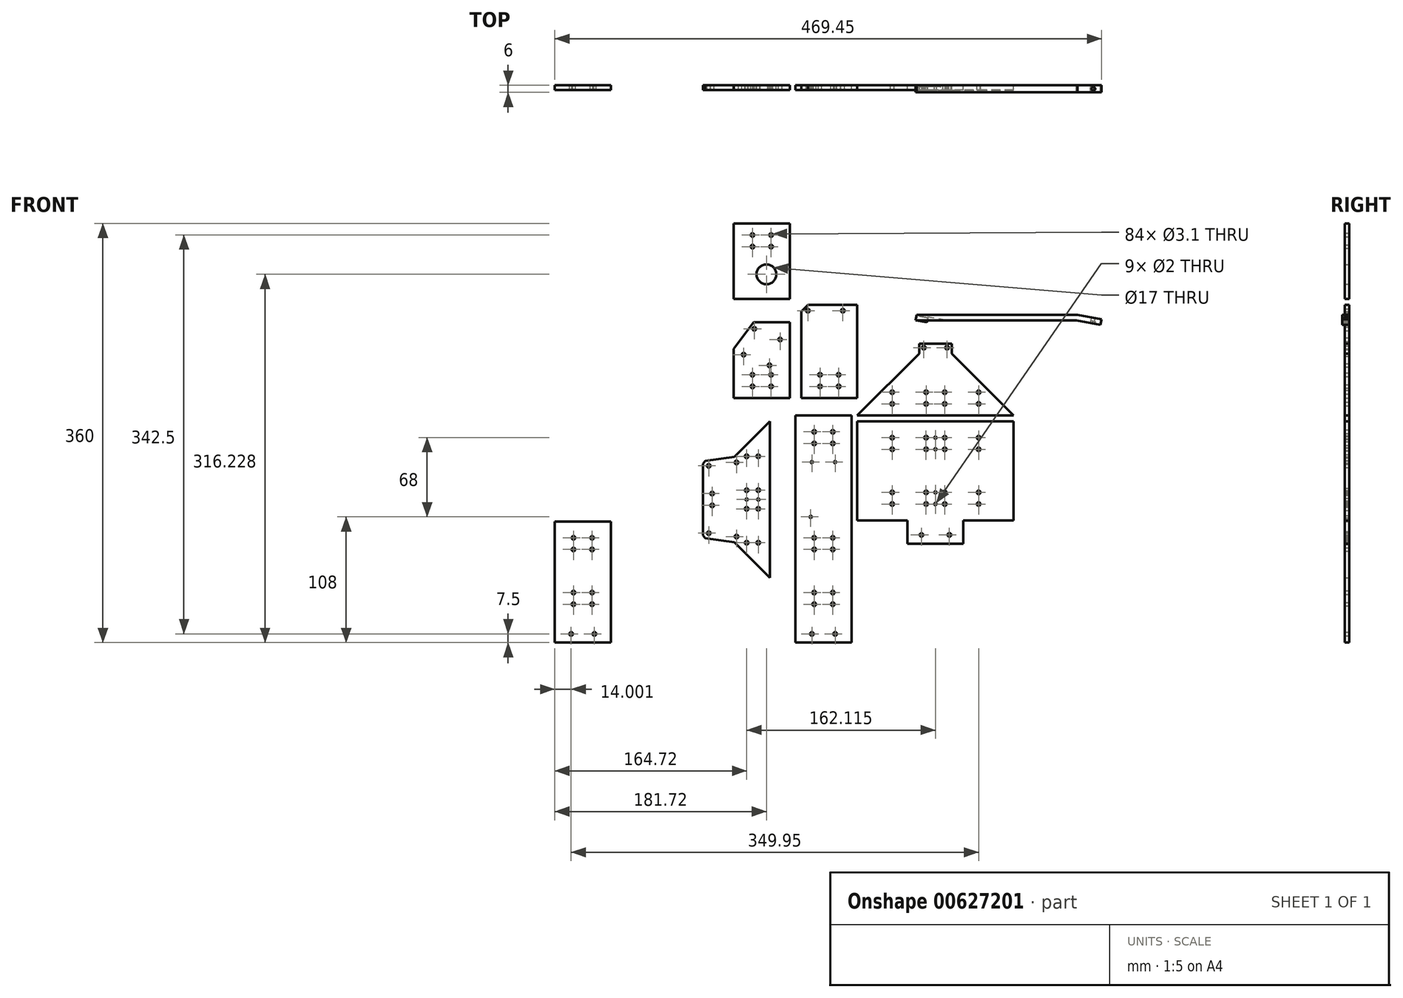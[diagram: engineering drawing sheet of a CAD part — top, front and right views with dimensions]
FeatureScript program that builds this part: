
annotation { "Feature Type Name" : "Feature", "Feature Type Description" : "" }
export const myFeature = defineFeature(function(context is Context, id is Id, definition is map)
    precondition{}
    {
        {
            var Q0;
            Q0=qCreatedBy(makeId("Front.planeOp"),FACE);
            var sketch = newSketch(context, id + "F0", { "sketchPlane" : qUnion([Q0])});
            skLineSegment(sketch, "E0", {"start": v(0, 93.11) * mm, "end": v(0, -84.87) * mm, "construction": true});
            skLineSegment(sketch, "E1", {"start": v(-96.99, 0) * mm, "end": v(119.24, 0) * mm, "construction": true});
            skLineSegment(sketch, "E2", {"start": v(0, 0) * mm, "end": v(134.2, 0) * mm});
            skLineSegment(sketch, "E3", {"start": v(81.12, 53.03) * mm, "end": v(134.2, 0) * mm});
            skLineSegment(sketch, "E4", {"start": v(81.12, 53.03) * mm, "end": v(81.12, 61.57) * mm});
            skLineSegment(sketch, "E5", {"start": v(81.12, 61.57) * mm, "end": v(53.12, 61.57) * mm});
            skLineSegment(sketch, "E6", {"start": v(53.12, 61.57) * mm, "end": v(53.12, 53.03) * mm});
            skLineSegment(sketch, "E7", {"start": v(53.12, 53.03) * mm, "end": v(0, 0) * mm});
            skCircle(sketch, "E8", {"center": v(57.12, 58.24) * mm, "radius": 1.55 * mm});
            skLineSegment(sketch, "E9", {"start": v(67.12, 61.57) * mm, "end": v(67.12, -9.5) * mm, "construction": true});
            skCircle(sketch, "E10.MirrorC", {"center": v(77.12, 58.24) * mm, "radius": 1.55 * mm});
            skCircle(sketch, "E11", {"center": v(59.12, 20) * mm, "radius": 1.55 * mm});
            skCircle(sketch, "E12", {"center": v(59.12, 10) * mm, "radius": 1.55 * mm});
            skCircle(sketch, "E13.MirrorC", {"center": v(75.12, 20) * mm, "radius": 1.55 * mm});
            skCircle(sketch, "E14.MirrorC", {"center": v(75.12, 10) * mm, "radius": 1.55 * mm});
            skCircle(sketch, "E15", {"center": v(30.01, 20) * mm, "radius": 1.55 * mm});
            skCircle(sketch, "E16", {"center": v(30.01, 10) * mm, "radius": 1.55 * mm});
            skCircle(sketch, "E17.MirrorC", {"center": v(104.22, 20) * mm, "radius": 1.55 * mm});
            skCircle(sketch, "E18.MirrorC", {"center": v(104.22, 10) * mm, "radius": 1.55 * mm});
            skLineSegment(sketch, "E19", {"start": v(0, -5) * mm, "end": v(134.2, -5) * mm});
            skLineSegment(sketch, "E20", {"start": v(134.2, -5) * mm, "end": v(134.2, -90) * mm});
            skLineSegment(sketch, "E21", {"start": v(134.2, -90) * mm, "end": v(91.1, -90) * mm});
            skLineSegment(sketch, "E22", {"start": v(91.1, -90) * mm, "end": v(91.1, -110) * mm});
            skLineSegment(sketch, "E23", {"start": v(91.1, -110) * mm, "end": v(43.1, -110) * mm});
            skLineSegment(sketch, "E24", {"start": v(43.1, -110) * mm, "end": v(43.1, -90) * mm});
            skLineSegment(sketch, "E25", {"start": v(43.1, -90) * mm, "end": v(0, -90) * mm});
            skLineSegment(sketch, "E26", {"start": v(0, -90) * mm, "end": v(0, -5) * mm});
            skCircle(sketch, "E27", {"center": v(30, -19) * mm, "radius": 1.55 * mm});
            skCircle(sketch, "E28", {"center": v(30, -29) * mm, "radius": 1.55 * mm});
            skCircle(sketch, "E29", {"center": v(30, -66) * mm, "radius": 1.55 * mm});
            skCircle(sketch, "E30", {"center": v(30, -76) * mm, "radius": 1.55 * mm});
            skCircle(sketch, "E31", {"center": v(59.1, -19) * mm, "radius": 1.55 * mm});
            skCircle(sketch, "E32", {"center": v(59.1, -29) * mm, "radius": 1.55 * mm});
            skLineSegment(sketch, "E33", {"start": v(67.12, -9.5) * mm, "end": v(67.12, -126.3) * mm, "construction": true});
            skCircle(sketch, "E34", {"center": v(67.12, -19) * mm, "radius": 1 * mm});
            skCircle(sketch, "E35", {"center": v(67.12, -29) * mm, "radius": 1 * mm});
            skCircle(sketch, "E36.MirrorC", {"center": v(75.13, -19) * mm, "radius": 1.55 * mm});
            skCircle(sketch, "E37.MirrorC", {"center": v(75.13, -29) * mm, "radius": 1.55 * mm});
            skCircle(sketch, "E38.MirrorC", {"center": v(104.23, -29) * mm, "radius": 1.55 * mm});
            skCircle(sketch, "E39.MirrorC", {"center": v(104.23, -19) * mm, "radius": 1.55 * mm});
            skCircle(sketch, "E40.MirrorC", {"center": v(104.23, -66) * mm, "radius": 1.55 * mm});
            skCircle(sketch, "E41.MirrorC", {"center": v(104.23, -76) * mm, "radius": 1.55 * mm});
            skCircle(sketch, "E42", {"center": v(59.1, -66) * mm, "radius": 1.55 * mm});
            skCircle(sketch, "E43", {"center": v(59.1, -76) * mm, "radius": 1.55 * mm});
            skCircle(sketch, "E44.MirrorC", {"center": v(75.13, -66) * mm, "radius": 1.55 * mm});
            skCircle(sketch, "E45.MirrorC", {"center": v(75.13, -76) * mm, "radius": 1.55 * mm});
            skCircle(sketch, "E46", {"center": v(67.12, -66) * mm, "radius": 1 * mm});
            skCircle(sketch, "E47", {"center": v(67.12, -76) * mm, "radius": 1 * mm});
            skCircle(sketch, "E48", {"center": v(79.1, -102.5) * mm, "radius": 1.55 * mm});
            skCircle(sketch, "E49.MirrorC", {"center": v(55.13, -102.5) * mm, "radius": 1.55 * mm});
            skLineSegment(sketch, "E50", {"start": v(-75, -5) * mm, "end": v(-75, -139.2) * mm});
            skLineSegment(sketch, "E51", {"start": v(-75, -5) * mm, "end": v(-105.4, -35.4) * mm});
            skLineSegment(sketch, "E52", {"start": v(-75, -72.1) * mm, "end": v(-229.8, -72.1) * mm, "construction": true});
            skPoint(sketch, "E52.endSnap0", {"position": v(-75, -72.1) * mm});
            skLineSegment(sketch, "E53", {"start": v(-105.4, -35.4) * mm, "end": v(-130.73, -38.96) * mm});
            skLineSegment(sketch, "E54", {"start": v(-130.73, -38.96) * mm, "end": v(-132.36, -41.48) * mm});
            skLineSegment(sketch, "E55.MirrorCS", {"start": v(-130.73, -105.24) * mm, "end": v(-132.36, -102.73) * mm});
            skLineSegment(sketch, "E56.MirrorCS", {"start": v(-105.4, -108.8) * mm, "end": v(-130.73, -105.24) * mm});
            skLineSegment(sketch, "E57.MirrorCS", {"start": v(-75, -139.2) * mm, "end": v(-105.4, -108.8) * mm});
            skLineSegment(sketch, "E58", {"start": v(-132.36, -102.73) * mm, "end": v(-132.36, -41.48) * mm});
            skCircle(sketch, "E59", {"center": v(-85, -35) * mm, "radius": 1.55 * mm});
            skCircle(sketch, "E60", {"center": v(-95, -35) * mm, "radius": 1.55 * mm});
            skCircle(sketch, "E61", {"center": v(-85, -64.1) * mm, "radius": 1.55 * mm});
            skCircle(sketch, "E62", {"center": v(-95, -64.1) * mm, "radius": 1.55 * mm});
            skCircle(sketch, "E63", {"center": v(-85, -72.1) * mm, "radius": 1 * mm});
            skCircle(sketch, "E64", {"center": v(-95, -72.1) * mm, "radius": 1 * mm});
            skCircle(sketch, "E65", {"center": v(-124.59, -67) * mm, "radius": 1.55 * mm});
            skCircle(sketch, "E66", {"center": v(-127.51, -43.18) * mm, "radius": 1.55 * mm});
            skLineSegment(sketch, "E67", {"start": v(-124.59, -67) * mm, "end": v(-110.64, -67) * mm, "construction": true});
            skLineSegment(sketch, "E68", {"start": v(-124.59, -67) * mm, "end": v(-127.51, -43.18) * mm, "construction": true});
            skLineSegment(sketch, "E69", {"start": v(-127.51, -43.18) * mm, "end": v(-96.66, -39.4) * mm, "construction": true});
            skCircle(sketch, "E70", {"center": v(-103.7, -40.26) * mm, "radius": 1.55 * mm});
            skCircle(sketch, "E71.MirrorC", {"center": v(-124.59, -77.2) * mm, "radius": 1.55 * mm});
            skCircle(sketch, "E72.MirrorC", {"center": v(-127.51, -101.03) * mm, "radius": 1.55 * mm});
            skCircle(sketch, "E73.MirrorC", {"center": v(-103.7, -103.95) * mm, "radius": 1.55 * mm});
            skCircle(sketch, "E74.MirrorC", {"center": v(-95, -80.1) * mm, "radius": 1.55 * mm});
            skCircle(sketch, "E75.MirrorC", {"center": v(-95, -109.2) * mm, "radius": 1.55 * mm});
            skCircle(sketch, "E76.MirrorC", {"center": v(-85, -109.2) * mm, "radius": 1.55 * mm});
            skCircle(sketch, "E77.MirrorC", {"center": v(-85, -80.1) * mm, "radius": 1.55 * mm});
            skLineSegment(sketch, "E78.bottom", {"start": v(0, 15) * mm, "end": v(-48, 15) * mm});
            skLineSegment(sketch, "E78.top", {"start": v(0, 95) * mm, "end": v(-48, 95) * mm});
            skLineSegment(sketch, "E78.left", {"start": v(0, 15) * mm, "end": v(0, 95) * mm});
            skLineSegment(sketch, "E78.right", {"start": v(-48, 15) * mm, "end": v(-48, 95) * mm});
            skCircle(sketch, "E79", {"center": v(-16, 25) * mm, "radius": 1.55 * mm});
            skLineSegment(sketch, "E80", {"start": v(-96.15, 55) * mm, "end": v(28.2, 55) * mm, "construction": true});
            skLineSegment(sketch, "E81", {"start": v(-24, 100.42) * mm, "end": v(-24, 7.26) * mm, "construction": true});
            skLineSegment(sketch, "E82", {"start": v(-42.4, 95) * mm, "end": v(-48, 89.4) * mm});
            skCircle(sketch, "E83", {"center": v(-42.4, 90) * mm, "radius": 1.55 * mm});
            skCircle(sketch, "E84", {"center": v(-12.4, 90) * mm, "radius": 1.55 * mm});
            skCircle(sketch, "E85", {"center": v(-16, 35) * mm, "radius": 1.55 * mm});
            skCircle(sketch, "E86.MirrorC", {"center": v(-32, 35) * mm, "radius": 1.55 * mm});
            skCircle(sketch, "E87.MirrorC", {"center": v(-32, 25) * mm, "radius": 1.55 * mm});
            skLineSegment(sketch, "E88.bottom", {"start": v(-53, 0) * mm, "end": v(-5, 0) * mm});
            skLineSegment(sketch, "E88.top", {"start": v(-53, -195) * mm, "end": v(-5, -195) * mm});
            skLineSegment(sketch, "E88.left", {"start": v(-53, 0) * mm, "end": v(-53, -195) * mm});
            skLineSegment(sketch, "E88.right", {"start": v(-5, 0) * mm, "end": v(-5, -195) * mm});
            skCircle(sketch, "E89", {"center": v(-21, -105) * mm, "radius": 1.55 * mm});
            skLineSegment(sketch, "E90", {"start": v(-29, 0) * mm, "end": v(-29, -227.99) * mm, "construction": true});
            skCircle(sketch, "E91", {"center": v(-21, -115) * mm, "radius": 1.55 * mm});
            skCircle(sketch, "E92", {"center": v(-21, -152) * mm, "radius": 1.55 * mm});
            skCircle(sketch, "E93", {"center": v(-21, -162) * mm, "radius": 1.55 * mm});
            skCircle(sketch, "E94", {"center": v(-19, -187.5) * mm, "radius": 1.55 * mm});
            skCircle(sketch, "E95", {"center": v(-40, -87) * mm, "radius": 1 * mm});
            skCircle(sketch, "E96", {"center": v(-21, -14) * mm, "radius": 1.55 * mm});
            skCircle(sketch, "E97", {"center": v(-21, -24) * mm, "radius": 1.55 * mm});
            skCircle(sketch, "E98", {"center": v(-19, -40) * mm, "radius": 1 * mm});
            skCircle(sketch, "E99.MirrorC", {"center": v(-39, -40) * mm, "radius": 1 * mm});
            skCircle(sketch, "E100.MirrorC", {"center": v(-37, -24) * mm, "radius": 1.55 * mm});
            skCircle(sketch, "E101.MirrorC", {"center": v(-37, -14) * mm, "radius": 1.55 * mm});
            skCircle(sketch, "E102.MirrorC", {"center": v(-37, -105) * mm, "radius": 1.55 * mm});
            skCircle(sketch, "E103.MirrorC", {"center": v(-37, -115) * mm, "radius": 1.55 * mm});
            skCircle(sketch, "E104.MirrorC", {"center": v(-37, -162) * mm, "radius": 1.55 * mm});
            skCircle(sketch, "E105.MirrorC", {"center": v(-37, -152) * mm, "radius": 1.55 * mm});
            skCircle(sketch, "E106.MirrorC", {"center": v(-39, -187.5) * mm, "radius": 1.55 * mm});
            skLineSegment(sketch, "E107.bottom", {"start": v(-58, 15) * mm, "end": v(-106, 15) * mm});
            skLineSegment(sketch, "E107.top", {"start": v(-58, 80) * mm, "end": v(-106, 80) * mm});
            skLineSegment(sketch, "E107.left", {"start": v(-58, 15) * mm, "end": v(-58, 80) * mm});
            skLineSegment(sketch, "E107.right", {"start": v(-106, 15) * mm, "end": v(-106, 80) * mm});
            skLineSegment(sketch, "E108", {"start": v(-82, 88.4) * mm, "end": v(-82, 7.1) * mm, "construction": true});
            skPoint(sketch, "E108.startSnap0", {"position": v(-82, 80) * mm});
            skCircle(sketch, "E109", {"center": v(-74, 25) * mm, "radius": 1.55 * mm});
            skCircle(sketch, "E110", {"center": v(-74, 35) * mm, "radius": 1.55 * mm});
            skLineSegment(sketch, "E111", {"start": v(-89, 80) * mm, "end": v(-106, 57.33) * mm});
            skCircle(sketch, "E112", {"center": v(-75.41, 43.1) * mm, "radius": 1.55 * mm});
            skCircle(sketch, "E113", {"center": v(-66.23, 65.26) * mm, "radius": 1.55 * mm});
            skCircle(sketch, "E114", {"center": v(-97.6, 52.28) * mm, "radius": 1.55 * mm});
            skCircle(sketch, "E115", {"center": v(-88.4, 74.45) * mm, "radius": 1.55 * mm});
            skCircle(sketch, "E116.MirrorC", {"center": v(-90, 35) * mm, "radius": 1.55 * mm});
            skCircle(sketch, "E117.MirrorC", {"center": v(-90, 25) * mm, "radius": 1.55 * mm});
            skLineSegment(sketch, "E118.bottom", {"start": v(-106, 15) * mm, "end": v(-58, 15) * mm});
            skLineSegment(sketch, "E119.bottom", {"start": v(-106, 100) * mm, "end": v(-58, 100) * mm});
            skLineSegment(sketch, "E119.top", {"start": v(-106, 165) * mm, "end": v(-58, 165) * mm});
            skLineSegment(sketch, "E119.left", {"start": v(-106, 100) * mm, "end": v(-106, 165) * mm});
            skLineSegment(sketch, "E119.right", {"start": v(-58, 100) * mm, "end": v(-58, 165) * mm});
            skLineSegment(sketch, "E120", {"start": v(-82, 175.23) * mm, "end": v(-82, 88.4) * mm, "construction": true});
            skPoint(sketch, "E120.startSnap0", {"position": v(-82, 165) * mm});
            skCircle(sketch, "E121", {"center": v(-74, 155) * mm, "radius": 1.55 * mm});
            skCircle(sketch, "E122.MirrorC", {"center": v(-90, 155) * mm, "radius": 1.55 * mm});
            skCircle(sketch, "E123", {"center": v(-74, 145) * mm, "radius": 1.55 * mm});
            skCircle(sketch, "E124.MirrorC", {"center": v(-90, 145) * mm, "radius": 1.55 * mm});
            skLineSegment(sketch, "E125", {"start": v(50.87, 86.5) * mm, "end": v(189.17, 86.5) * mm});
            skLineSegment(sketch, "E126", {"start": v(189.17, 86.5) * mm, "end": v(188.3, 81.57) * mm});
            skLineSegment(sketch, "E127", {"start": v(188.3, 81.57) * mm, "end": v(50, 81.57) * mm});
            skLineSegment(sketch, "E128", {"start": v(50, 81.57) * mm, "end": v(50.87, 86.5) * mm});
            skLineSegment(sketch, "E129", {"start": v(50.43, 84.03) * mm, "end": v(202.84, 84.03) * mm});
            skLineSegment(sketch, "E130", {"start": v(189.17, 86.5) * mm, "end": v(202.84, 84.03) * mm});
            skLineSegment(sketch, "E131", {"start": v(202.84, 84.03) * mm, "end": v(209.73, 82.79) * mm});
            skLineSegment(sketch, "E132", {"start": v(209.73, 82.79) * mm, "end": v(208.87, 77.86) * mm});
            skLineSegment(sketch, "E133", {"start": v(208.87, 77.86) * mm, "end": v(188.3, 81.57) * mm});
            skLineSegment(sketch, "E134.MirrorCS", {"start": v(-211.72, -195) * mm, "end": v(-259.72, -195) * mm});
            skCircle(sketch, "E135.MirrorC", {"center": v(-227.72, -152) * mm, "radius": 1.55 * mm});
            skCircle(sketch, "E136.MirrorC", {"center": v(-227.72, -162) * mm, "radius": 1.55 * mm});
            skCircle(sketch, "E137.MirrorC", {"center": v(-225.72, -187.5) * mm, "radius": 1.55 * mm});
            skCircle(sketch, "E138.MirrorC", {"center": v(-245.72, -187.5) * mm, "radius": 1.55 * mm});
            skCircle(sketch, "E139.MirrorC", {"center": v(-243.72, -152) * mm, "radius": 1.55 * mm});
            skCircle(sketch, "E140.MirrorC", {"center": v(-227.72, -105) * mm, "radius": 1.55 * mm});
            skCircle(sketch, "E141.MirrorC", {"center": v(-227.72, -115) * mm, "radius": 1.55 * mm});
            skCircle(sketch, "E142.MirrorC", {"center": v(-243.72, -115) * mm, "radius": 1.55 * mm});
            skCircle(sketch, "E143.MirrorC", {"center": v(-243.72, -105) * mm, "radius": 1.55 * mm});
            skCircle(sketch, "E144.MirrorC", {"center": v(-243.72, -162) * mm, "radius": 1.55 * mm});
            skLineSegment(sketch, "E145", {"start": v(-211.72, -195) * mm, "end": v(-211.72, -91) * mm});
            skLineSegment(sketch, "E146", {"start": v(-259.72, -195) * mm, "end": v(-259.72, -91) * mm});
            skLineSegment(sketch, "E147", {"start": v(-259.72, -91) * mm, "end": v(-211.72, -91) * mm});
            skCircle(sketch, "E148", {"center": v(-78, 121.23) * mm, "radius": 8.5 * mm});
            skSolve(sketch);
        }
        {
            var Q0;
            Q0=makeQuery(id+"F0.imprint","IMPRINT",FACE,{"disambiguationData":[TD([[makeQuery(id+"F0.imprint","IMPRINT",EDGE,{"derivedFrom":sQuery(id+"F0.wireOp",EDGE,"E19")}),-1.0]])]});
            var Q1;
            Q1=makeQuery(id+"F0.imprint","IMPRINT",FACE,{"disambiguationData":[TD([[makeQuery(id+"F0.imprint","IMPRINT",EDGE,{"derivedFrom":sQuery(id+"F0.wireOp",EDGE,"E2")}),1.0]])]});
            var Q2;
            Q2=makeQuery(id+"F0.imprint","IMPRINT",FACE,{"disambiguationData":[TD([[makeQuery(id+"F0.imprint","IMPRINT",EDGE,{"derivedFrom":sQuery(id+"F0.wireOp",EDGE,"E50")}),-1.0]])]});
            extrude(context, id + "F1", {"entities" : qUnion([Q0, Q1, Q2]), "depth" : 4 * mm, "offsetDistance" : 25 * mm});
        }
        {
            var Q0;
            {var subQ1=sQuery(id+"F0.wireOp",EDGE,"E78.bottom");Q0=makeQuery(id+"F0.imprint","IMPRINT",FACE,{"disambiguationData":[TD([[makeQuery(id+"F0.imprint","IMPRINT",EDGE,{"derivedFrom":subQ1}),-1.0]])]});}
            extrude(context, id + "F2", {"entities" : qUnion([Q0]), "depth" : 4 * mm, "offsetDistance" : 25 * mm});
        }
        {
            var Q0;
            Q0=makeQuery(id+"F0.imprint","IMPRINT",FACE,{"disambiguationData":[TD([[makeQuery(id+"F0.imprint","IMPRINT",EDGE,{"derivedFrom":sQuery(id+"F0.wireOp",EDGE,"E88.bottom")}),-1.0]])]});
            extrude(context, id + "F3", {"entities" : qUnion([Q0]), "depth" : 4 * mm, "offsetDistance" : 25 * mm});
        }
        {
            var Q0;
            Q0=makeQuery(id+"F0.imprint","IMPRINT",FACE,{"disambiguationData":[TD([[makeQuery(id+"F0.imprint","IMPRINT",EDGE,{"derivedFrom":sQuery(id+"F0.wireOp",EDGE,"E118.bottom")}),-1.0]])]});
            var Q1;
            {var subQ1=sQuery(id+"F0.wireOp",EDGE,"E107.left");Q1=makeQuery(id+"F0.imprint","IMPRINT",FACE,{"disambiguationData":[TD([[makeQuery(id+"F0.imprint","IMPRINT",EDGE,{"derivedFrom":subQ1}),1.0]])]});}
            extrude(context, id + "F4", {"entities" : qUnion([Q0, Q1]), "depth" : 4 * mm, "offsetDistance" : 25 * mm});
        }
        {
            var Q0;
            Q0=makeQuery(id+"F0.imprint","IMPRINT",FACE,{"disambiguationData":[TD([[makeQuery(id+"F0.imprint","IMPRINT",EDGE,{"derivedFrom":sQuery(id+"F0.wireOp",EDGE,"E119.bottom")}),1.0]])]});
            extrude(context, id + "F5", {"entities" : qUnion([Q0]), "depth" : 4 * mm, "offsetDistance" : 25 * mm});
        }
        {
            var Q0;
            {var subQ0=sQuery(id+"F0.wireOp",EDGE,"E125");Q0=makeQuery(id+"F0.imprint","IMPRINT",FACE,{"disambiguationData":[TD([[makeQuery(id+"F0.imprint","IMPRINT",EDGE,{"derivedFrom":subQ0}),-1.0]])]});}
            var Q1;
            {var subQ0=sQuery(id+"F0.wireOp",EDGE,"E127");Q1=makeQuery(id+"F0.imprint","IMPRINT",FACE,{"disambiguationData":[TD([[makeQuery(id+"F0.imprint","IMPRINT",EDGE,{"derivedFrom":subQ0}),-1.0]])]});}
            var Q2;
            {var subQ0=sQuery(id+"F0.wireOp",EDGE,"E131");Q2=makeQuery(id+"F0.imprint","IMPRINT",FACE,{"disambiguationData":[TD([[makeQuery(id+"F0.imprint","IMPRINT",EDGE,{"derivedFrom":subQ0}),-1.0]])]});}
            var Q3;
            {var subQ0=sQuery(id+"F0.wireOp",EDGE,"E130");Q3=makeQuery(id+"F0.imprint","IMPRINT",FACE,{"disambiguationData":[TD([[makeQuery(id+"F0.imprint","IMPRINT",EDGE,{"derivedFrom":subQ0}),-1.0]])]});}
            extrude(context, id + "F6", {"entities" : qUnion([Q0, Q1, Q2, Q3]), "depth" : 6 * mm, "offsetDistance" : 25 * mm});
        }
        {
            var Q0;
            Q0=makeQuery(id+"F6.opExtrude","SWEPT_FACE",FACE,{"disambiguationData":[OSD([sQuery(id+"F0.wireOp",EDGE,"E130"),sQuery(id+"F0.wireOp",EDGE,"E131")])]});
            var sketch = newSketch(context, id + "F7", { "sketchPlane" : qUnion([Q0])});
            skLineSegment(sketch, "E149", {"start": v(191.75, -3) * mm, "end": v(167.13, -3) * mm, "construction": true});
            skCircle(sketch, "E150", {"center": v(184.75, -3) * mm, "radius": 1.55 * mm});
            skCircle(sketch, "E151", {"center": v(184.75, -3) * mm, "radius": 2.5 * mm});
            skSolve(sketch);
        }
        {
            var Q0;
            Q0=makeQuery(id+"F7.imprint","IMPRINT",FACE,{"disambiguationData":[TD([[makeQuery(id+"F7.imprint","IMPRINT",EDGE,{"derivedFrom":sQuery(id+"F7.wireOp",EDGE,"E150")}),1.0]])]});
            extrude(context, id + "F8", {"entities" : qUnion([Q0]), "operationType" : NewBodyOperationType.REMOVE, "oppositeDirection" : true, "depth" : 6 * mm, "offsetDistance" : 25 * mm});
        }
        {
            var Q0;
            Q0=makeQuery(id+"F6.opExtrude","SWEPT_FACE",FACE,{"disambiguationData":[OSD([sQuery(id+"F0.wireOp",EDGE,"E128")])]});
            var sketch = newSketch(context, id + "F9", { "sketchPlane" : qUnion([Q0])});
            skLineSegment(sketch, "E152", {"start": v(3, 89.01) * mm, "end": v(3, 97.59) * mm, "construction": true});
            skPoint(sketch, "E152.endSnap0", {"position": v(3, 94.01) * mm});
            skCircle(sketch, "E153", {"center": v(3, 91.51) * mm, "radius": 1.55 * mm});
            skCircle(sketch, "E154", {"center": v(3, 91.51) * mm, "radius": 2.25 * mm});
            skCircle(sketch, "E155", {"center": v(3, 91.51) * mm, "radius": 2.38 * mm});
            skSolve(sketch);
        }
        {
            var Q0;
            Q0=makeQuery(id+"F9.imprint","IMPRINT",FACE,{"disambiguationData":[TD([[makeQuery(id+"F9.imprint","IMPRINT",EDGE,{"derivedFrom":sQuery(id+"F9.wireOp",EDGE,"E153")}),1.0]])]});
            extrude(context, id + "F10", {"entities" : qUnion([Q0]), "operationType" : NewBodyOperationType.REMOVE, "oppositeDirection" : true, "depth" : 25 * mm, "offsetDistance" : 25 * mm});
        }
        {
            var Q0;
            Q0=makeQuery(id+"F9.imprint","IMPRINT",FACE,{"disambiguationData":[TD([[makeQuery(id+"F9.imprint","IMPRINT",EDGE,{"derivedFrom":sQuery(id+"F9.wireOp",EDGE,"E153")}),-1.0]])]});
            extrude(context, id + "F11", {"entities" : qUnion([Q0]), "operationType" : NewBodyOperationType.REMOVE, "oppositeDirection" : true, "depth" : 30 * mm, "offsetDistance" : 25 * mm});
        }
        {
            var Q0;
            Q0=makeQuery(id+"F9.imprint","IMPRINT",FACE,{"disambiguationData":[TD([[makeQuery(id+"F9.imprint","IMPRINT",EDGE,{"derivedFrom":sQuery(id+"F9.wireOp",EDGE,"E153")}),-1.0]])]});
            var Q1;
            Q1=makeQuery(id+"F9.imprint","IMPRINT",FACE,{"disambiguationData":[TD([[makeQuery(id+"F9.imprint","IMPRINT",EDGE,{"derivedFrom":sQuery(id+"F9.wireOp",EDGE,"E154")}),-1.0]])]});
            extrude(context, id + "F12", {"entities" : qUnion([Q0, Q1]), "operationType" : NewBodyOperationType.ADD, "oppositeDirection" : true, "depth" : 10 * mm, "offsetDistance" : 25 * mm});
        }
        {
            var Q0;
            Q0=makeQuery(id+"F6.opExtrude","SWEPT_FACE",FACE,{"disambiguationData":[OSD([sQuery(id+"F0.wireOp",EDGE,"E133")])]});
            var sketch = newSketch(context, id + "F13", { "sketchPlane" : qUnion([Q0])});
            skCircle(sketch, "E156.cCircle", {"center": v(184.75, 3) * mm, "radius": 2 * mm, "construction": true});
            skLineSegment(sketch, "E156.0", {"start": v(182.75, 1.85) * mm, "end": v(182.75, 4.15) * mm});
            skLineSegment(sketch, "E156.1", {"start": v(182.75, 4.15) * mm, "end": v(184.75, 5.3) * mm});
            skLineSegment(sketch, "E156.2", {"start": v(184.75, 5.3) * mm, "end": v(186.75, 4.15) * mm});
            skLineSegment(sketch, "E156.3", {"start": v(186.75, 4.15) * mm, "end": v(186.75, 1.85) * mm});
            skLineSegment(sketch, "E156.4", {"start": v(186.75, 1.85) * mm, "end": v(184.75, 0.7) * mm});
            skLineSegment(sketch, "E156.5", {"start": v(184.75, 0.7) * mm, "end": v(182.75, 1.85) * mm});
            skPoint(sketch, "E156.0.midPoint", {"position": v(182.75, 3) * mm});
            skSolve(sketch);
        }
        {
            var Q0;
            Q0=makeQuery(id+"F13.imprint","IMPRINT",FACE,{"disambiguationData":[TD([[makeQuery(id+"F13.imprint","IMPRINT",EDGE,{"derivedFrom":sQuery(id+"F13.wireOp",EDGE,"E156.0")}),-1.0]])]});
            extrude(context, id + "F14", {"entities" : qUnion([Q0]), "operationType" : NewBodyOperationType.REMOVE, "oppositeDirection" : true, "depth" : 2 * mm, "offsetDistance" : 25 * mm});
        }
        {
            var Q0;
            Q0=makeQuery(id+"F0.imprint","IMPRINT",FACE,{"disambiguationData":[TD([[makeQuery(id+"F0.imprint","IMPRINT",EDGE,{"derivedFrom":sQuery(id+"F0.wireOp",EDGE,"E134.MirrorCS")}),-1.0]])]});
            extrude(context, id + "F15", {"entities" : qUnion([Q0]), "depth" : 4 * mm, "offsetDistance" : 25 * mm});
        }
    });
